# Revit family: Baby Change Station_Metlam_Horizontal_Surface Mounted
name_source: partatom
category: Specialty Equipment
revit_build: Autodesk Revit 2016 (Build: 20170117_1200(x64)
units: mm (PartAtom-declared; Revit-internal decimal feet)

## family parameters
Always vertical = Yes
Cut with Voids When Loaded = No
OmniClass Number = 23.40.20.21.37
OmniClass Title = Diaper Changing Units
Part Type = Normal
Room Calculation Point = Yes
Round Connector Dimension = Use Diameter
Shared = No
Work Plane-Based = No

## types (1)
- 855w x 495d x 560h (ML_8100H)
    Description = Metlam Horizontal Baby Change Station
    Frame_Material = z_Metlam_Metal_Stainless Steel_Satin
    Manufacturer = Metlam
    Manufacturer_Overall Depth = 495 mm  [stored 1.62402 ft]
    Manufacturer_Overall Height = 560 mm  [stored 1.83727 ft]
    Manufacturer_Overall Width = 855 mm  [stored 2.80512 ft]
    Manufacturer_Spec Code = ML_8100H
    Manufacturer_URL__Product Specific = https://www.metlam.com.au
    Material_ANZRS = z_Metlam_White
    Model = ML_8100H
    Type Comments = Baby Change Tables
    URL = http://www.metlam.com.au

note: [stored X ft] marks values corroborated as IEEE doubles in the binary element streams (Revit-internal decimal feet)

## geometry (parser evidence)
native form markers: Sweep x2
no freeform markers — native parametric forms only
